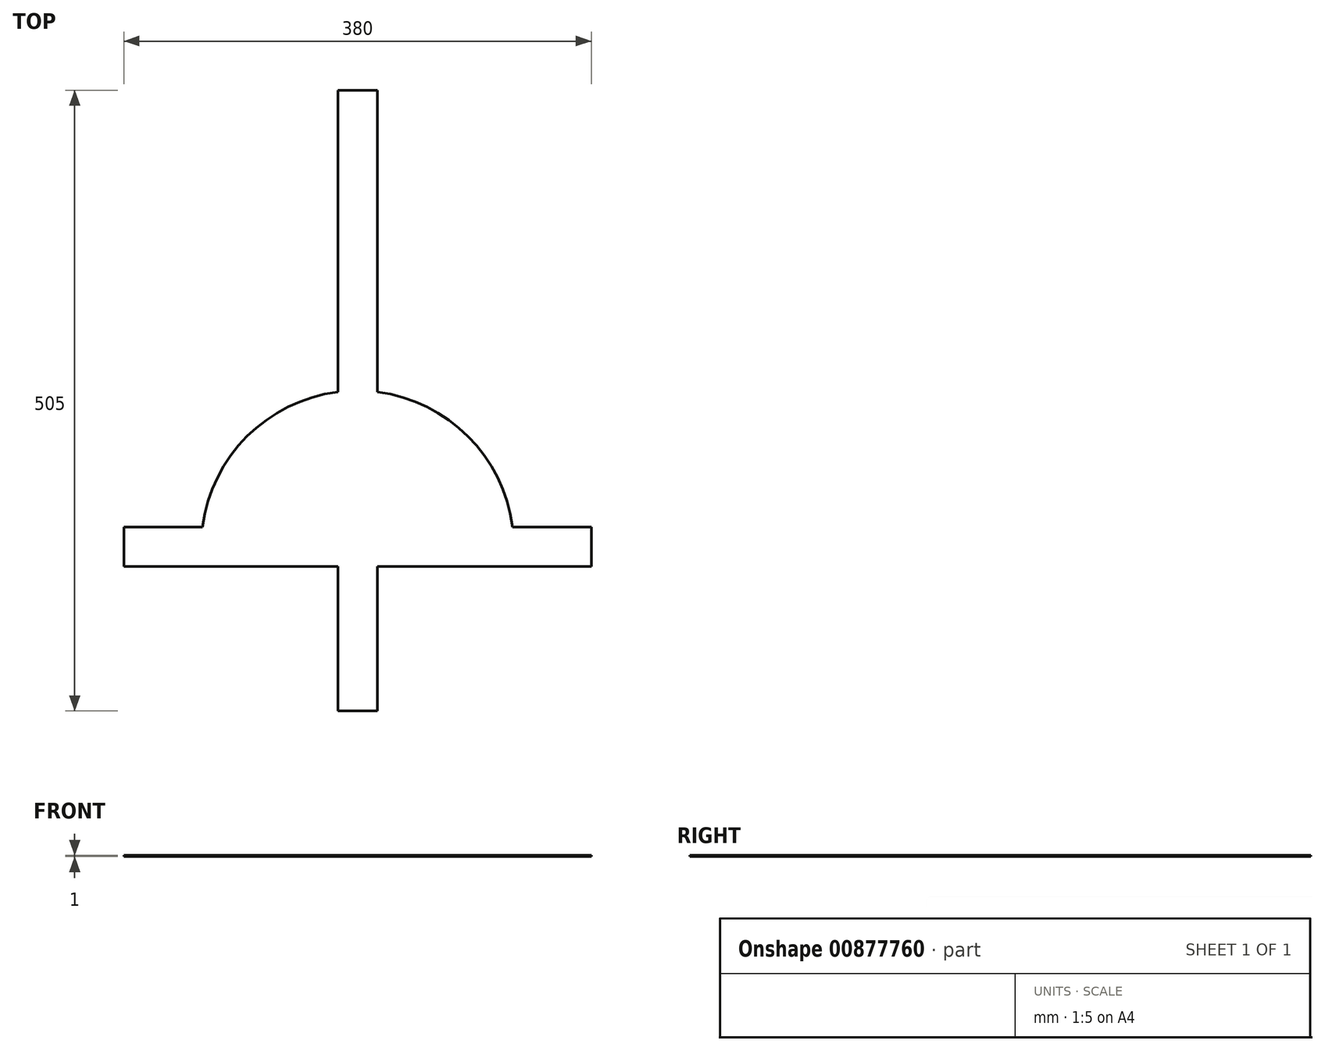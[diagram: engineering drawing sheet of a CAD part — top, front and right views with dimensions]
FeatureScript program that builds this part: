
annotation { "Feature Type Name" : "Feature", "Feature Type Description" : "" }
export const myFeature = defineFeature(function(context is Context, id is Id, definition is map)
    precondition{}
    {
        {
            var Q0;
            Q0=qCreatedBy(makeId("Top.planeOp"),FACE);
            var sketch = newSketch(context, id + "F0", { "sketchPlane" : qUnion([Q0])});
            skArc(sketch, "E0", {"start": v(-125.99, 16) * mm, "mid": v(-89.8, 89.8) * mm, "end": v(-16, 125.99) * mm});
            skLineSegment(sketch, "E1", {"start": v(-190, 16) * mm, "end": v(-190, 0) * mm});
            skLineSegment(sketch, "E2.MirrorCS", {"start": v(-16, -16) * mm, "end": v(-190, -16) * mm});
            skLineSegment(sketch, "E3.MirrorCS", {"start": v(-190, -16) * mm, "end": v(-190, 0) * mm});
            skLineSegment(sketch, "E4.MirrorCS", {"start": v(190, 16) * mm, "end": v(190, 0) * mm});
            skLineSegment(sketch, "E5.MirrorCS", {"start": v(190, -16) * mm, "end": v(190, 0) * mm});
            skLineSegment(sketch, "E6.MirrorCS", {"start": v(16, -16) * mm, "end": v(190, -16) * mm});
            skArc(sketch, "E7.MirrorCS", {"start": v(125.99, 16) * mm, "mid": v(89.8, 89.8) * mm, "end": v(16, 125.99) * mm});
            skPoint(sketch, "E8.orphan", {"position": v(-98, 0) * mm});
            skPoint(sketch, "E9.orphan", {"position": v(-127, 0) * mm});
            skPoint(sketch, "E10.orphan", {"position": v(98, 0) * mm});
            skPoint(sketch, "E11.orphan", {"position": v(127, 0) * mm});
            skLineSegment(sketch, "E12.trimOffspring", {"start": v(125.99, 16) * mm, "end": v(190, 16) * mm});
            skLineSegment(sketch, "E13.trimOffspring", {"start": v(-125.99, 16) * mm, "end": v(-190, 16) * mm});
            skLineSegment(sketch, "E14", {"start": v(-16, 371.41) * mm, "end": v(-16, 125.99) * mm});
            skLineSegment(sketch, "E15", {"start": v(-16, -133.59) * mm, "end": v(0, -133.59) * mm});
            skLineSegment(sketch, "E16", {"start": v(-16, 371.41) * mm, "end": v(0, 371.41) * mm});
            skLineSegment(sketch, "E17.MirrorCS", {"start": v(16, 371.41) * mm, "end": v(16, 125.99) * mm});
            skLineSegment(sketch, "E18.MirrorCS", {"start": v(16, -133.59) * mm, "end": v(0, -133.59) * mm});
            skLineSegment(sketch, "E19.MirrorCS", {"start": v(16, 371.41) * mm, "end": v(0, 371.41) * mm});
            skPoint(sketch, "E20.orphan", {"position": v(0, 127) * mm});
            skPoint(sketch, "E21.orphan", {"position": v(0, 98) * mm});
            skLineSegment(sketch, "E22.trimOffspring", {"start": v(-16, -16) * mm, "end": v(-16, -133.59) * mm});
            skLineSegment(sketch, "E23.trimOffspring", {"start": v(16, -16) * mm, "end": v(16, -133.59) * mm});
            skPoint(sketch, "E24.MirrorCS.start.orphan", {"position": v(0, 16) * mm});
            skPoint(sketch, "E25.orphan", {"position": v(0, -16) * mm});
            skSolve(sketch);
        }
        {
            var Q0;
            Q0 = qSketchRegion(id + "F0", true);
            extrude(context, id + "F1", {"entities" : qUnion([Q0]), "depth" : 1 * mm, "offsetDistance" : 25 * mm});
        }
    });
